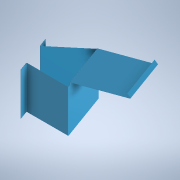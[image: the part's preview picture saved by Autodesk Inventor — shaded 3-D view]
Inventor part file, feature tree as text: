
AUTODESK INVENTOR PART (.ipt)
format: ipt  version: 2022 (Build 260153000, 153)  size: 261,632 bytes
history: native  units: mm
features: sketch x7, sheet_metal_op x7, other x2, plane x1
ambient origin geometry x8: Origin, YZ Plane, XZ Plane, XY Plane, X Axis, Y Axis, Z Axis, Center Point
bodies: Solid1 (feature_tree)
feature tree (17):
  sketch  "Sketch1"  dims[d0=1800.0mm]
  sheet_metal_op  "Face1"
  sketch  "Sketch3"  dims[d2=3.048mm]
  sheet_metal_op  "Fold1"
  sheet_metal_op  "Fold2"
  sketch  "Sketch4"  dims[d3=300.0mm]
  sheet_metal_op  "Fold3"
  sheet_metal_op  "Fold4"
  sketch  "Sketch5"  dims[d4=490.0mm]
  plane  "Work Plane1"
  sheet_metal_op  "Fold7"
  sheet_metal_op  "Fold8"
  sketch  "Sketch2"  dims[d1=500.0mm]
  other  "Plate1"
  sketch  "Sketch8"  dims[d5=3.048mm]
  sketch  "Sketch9"  dims[d6=1.524mm d7=6.096mm d8=3.048mm d9=19.198622mm d10=3.048mm d11=3.048mm d12=1.524mm d13=6.096mm d14=3.048mm d15=19.198622mm d16=3.048mm d17=110.0mm d18=490.0mm d19=90.0deg d20=3.048mm d21=1.524mm d22=6.096mm d23=3.048mm d24=19.198622mm d25=3.048mm d26=3.048mm d27=1.524mm d28=6.096mm d29=3.048mm d30=19.198622mm d31=3.048mm d32=270.0mm d33=540.0mm d34=632.0mm d49=20.0mm d50=20.0mm d51=5.0mm d52=3.048mm d53=1.524mm d54=6.096mm d55=3.048mm d56=90.0deg d57=3.048mm d58=50.0mm d59=3.048mm d60=1.524mm d61=6.096mm d62=3.048mm d63=22.68928mm d64=3.048mm]
  other  "Definition1"
